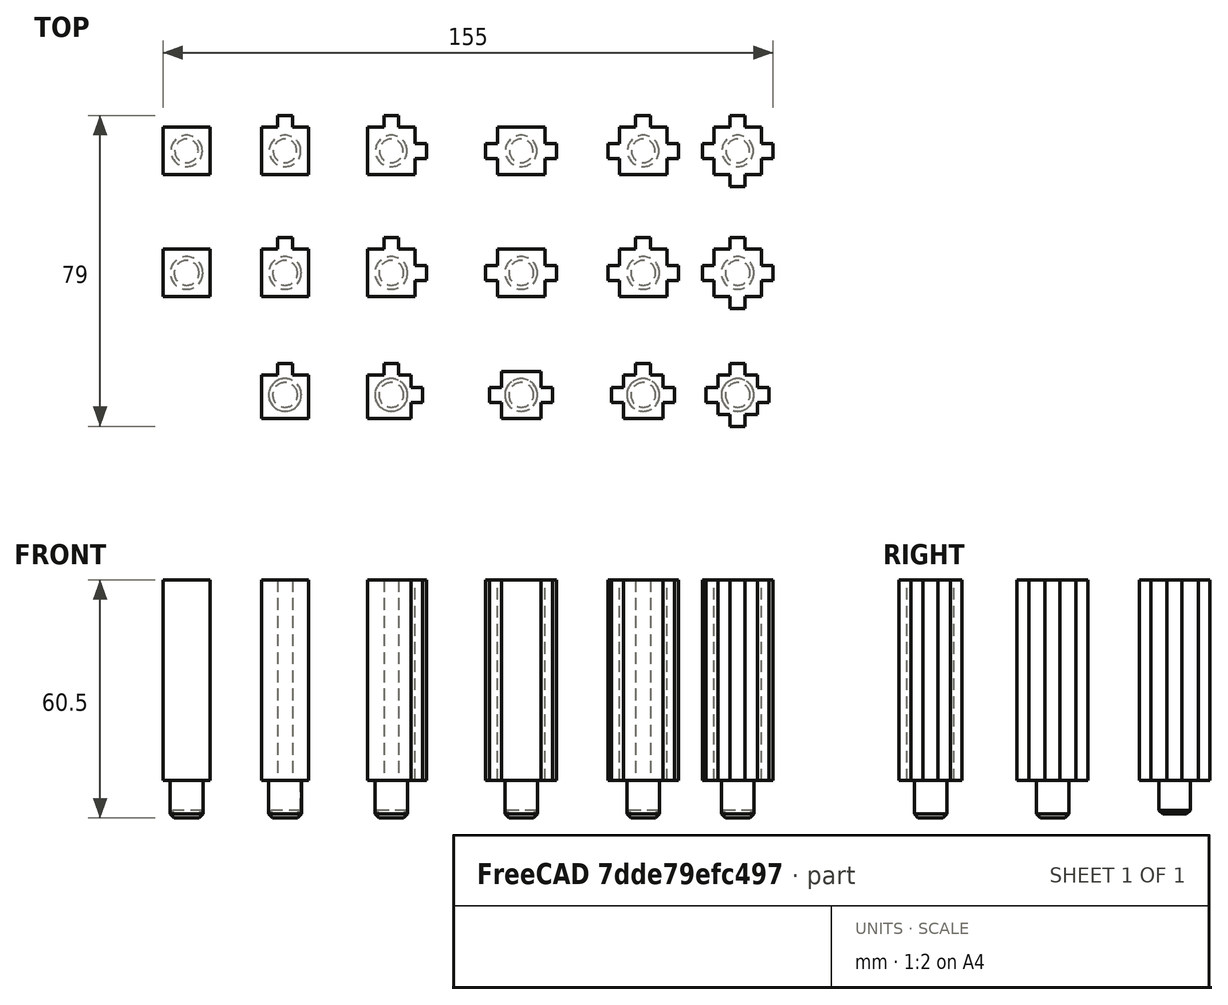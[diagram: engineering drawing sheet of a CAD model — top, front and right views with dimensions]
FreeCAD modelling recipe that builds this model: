
FCSTD DOCUMENT  (FreeCAD 0.18R16110 (Git))
Label: poste
License: All rights reserved
LicenseURL: http://en.wikipedia.org/wiki/All_rights_reserved
objects: Part::Box×53, Part::Cylinder×17, Part::Chamfer×17, Part::MultiFuse×17
note: 104 computed .brp shape members not serialized (recipe doc carries the construction recipe); baked Part::Feature solids carry a one-line shape summary decoded from their .brp

FEATURE [Part::Box] Box  label="Cubo"
  AttacherType = Attacher::AttachEngine3D
  Height = 51
  Length = 12
  Width = 12
FEATURE [Part::Box] Box002  label="Cubo002"
  AttacherType = Attacher::AttachEngine3D
  Height = 51
  Length = 3.8
  Placement = pos=(4.1,11,0) rot=(0,0,1;0rad)
  Width = 4
FEATURE [Part::Box] Box003  label="Cubo003"
  AttacherType = Attacher::AttachEngine3D
  Height = 51
  Length = 4
  Placement = pos=(-3,4.1,0) rot=(0,0,1;0rad)
  Width = 3.8
FEATURE [Part::Box] Box004  label="Cubo004"
  AttacherType = Attacher::AttachEngine3D
  Height = 51
  Length = 4
  Placement = pos=(11,4.1,0) rot=(0,0,1;0rad)
  Width = 3.8
FEATURE [Part::Cylinder] Cylinder  label="Cilindro"
  Angle = 360
  AttacherType = Attacher::AttachEngine3D
  Height = 9
  Placement = pos=(6,6,-8.5) rot=(0,0,1;0rad)
  Radius = 4
FEATURE [Part::Chamfer] Chamfer
  Base = -> Cylinder
  Edges = 1 edges r=1: [Edge3]
FEATURE [Part::MultiFuse] Fusion  label="A8_poste_3_paredes"
  Placement = pos=(27,0,0) rot=(0,0,1;0rad)
  Shapes = -> [Box,Box003,Box002,Box004,Chamfer]
FEATURE [Part::Box] Box005  label="Cubo005"
  AttacherType = Attacher::AttachEngine3D
  Height = 51
  Length = 12
  Width = 12
FEATURE [Part::Cylinder] Cylinder001  label="Cilindro001"
  Angle = 360
  AttacherType = Attacher::AttachEngine3D
  Height = 9
  Placement = pos=(6,6,-8.5) rot=(0,0,1;0rad)
  Radius = 4
FEATURE [Part::Box] Box006  label="Cubo006"
  AttacherType = Attacher::AttachEngine3D
  Height = 51
  Length = 3.8
  Placement = pos=(4.1,-3,0) rot=(0,0,1;0rad)
  Width = 4
FEATURE [Part::Box] Box007  label="Cubo007"
  AttacherType = Attacher::AttachEngine3D
  Height = 51
  Length = 4
  Placement = pos=(-3,4.1,0) rot=(0,0,1;0rad)
  Width = 3.8
FEATURE [Part::Box] Box008  label="Cubo008"
  AttacherType = Attacher::AttachEngine3D
  Height = 51
  Length = 3.8
  Placement = pos=(4.1,11,0) rot=(0,0,1;0rad)
  Width = 4
FEATURE [Part::Box] Box009  label="Cubo009"
  AttacherType = Attacher::AttachEngine3D
  Height = 51
  Length = 4
  Placement = pos=(11,4.1,0) rot=(0,0,1;0rad)
  Width = 3.8
FEATURE [Part::Chamfer] Chamfer001
  Base = -> Cylinder001
  Edges = 1 edges r=1: [Edge3]
FEATURE [Part::MultiFuse] Fusion001  label="A8_poste_4_paredes"
  Placement = pos=(51,0,0) rot=(0,0,1;0rad)
  Shapes = -> [Box005,Box006,Box007,Box008,Box009,Chamfer001]
FEATURE [Part::Box] Box010  label="Cubo010"
  AttacherType = Attacher::AttachEngine3D
  Height = 51
  Length = 12
  Width = 12
FEATURE [Part::Cylinder] Cylinder002  label="Cilindro002"
  Angle = 360
  AttacherType = Attacher::AttachEngine3D
  Height = 9
  Placement = pos=(6,6,-8.5) rot=(0,0,1;0rad)
  Radius = 4
FEATURE [Part::Box] Box012  label="Cubo012"
  AttacherType = Attacher::AttachEngine3D
  Height = 51
  Length = 3.8
  Placement = pos=(4.1,11,0) rot=(0,0,1;0rad)
  Width = 4
FEATURE [Part::Box] Box013  label="Cubo013"
  AttacherType = Attacher::AttachEngine3D
  Height = 51
  Length = 4
  Placement = pos=(11,4.1,0) rot=(0,0,1;0rad)
  Width = 3.8
FEATURE [Part::Chamfer] Chamfer002
  Base = -> Cylinder002
  Edges = 1 edges r=1: [Edge3]
FEATURE [Part::MultiFuse] Fusion002  label="A8_poste_2_paredes_esquina"
  Placement = pos=(-37,0,0) rot=(0,0,1;0rad)
  Shapes = -> [Box010,Box012,Box013,Chamfer002]
FEATURE [Part::Box] Box014  label="Cubo014"
  AttacherType = Attacher::AttachEngine3D
  Height = 51
  Length = 12
  Width = 12
FEATURE [Part::Cylinder] Cylinder003  label="Cilindro003"
  Angle = 360
  AttacherType = Attacher::AttachEngine3D
  Height = 9
  Placement = pos=(6,6,-8.5) rot=(0,0,1;0rad)
  Radius = 4
FEATURE [Part::Box] Box015  label="Cubo015"
  AttacherType = Attacher::AttachEngine3D
  Height = 51
  Length = 4
  Placement = pos=(-3,4.1,0) rot=(0,0,1;0rad)
  Width = 3.8
FEATURE [Part::Box] Box017  label="Cubo017"
  AttacherType = Attacher::AttachEngine3D
  Height = 51
  Length = 4
  Placement = pos=(11,4.1,0) rot=(0,0,1;0rad)
  Width = 3.8
FEATURE [Part::Chamfer] Chamfer003
  Base = -> Cylinder003
  Edges = 1 edges r=1: [Edge3]
FEATURE [Part::MultiFuse] Fusion003  label="A8_poste_2_paredes_linea"
  Placement = pos=(-4,0,0) rot=(0,0,1;0rad)
  Shapes = -> [Box014,Box015,Box017,Chamfer003]
FEATURE [Part::Box] Box018  label="Cubo018"
  AttacherType = Attacher::AttachEngine3D
  Height = 51
  Length = 12
  Width = 12
FEATURE [Part::Cylinder] Cylinder004  label="Cilindro004"
  Angle = 360
  AttacherType = Attacher::AttachEngine3D
  Height = 9
  Placement = pos=(6,6,-8.5) rot=(0,0,1;0rad)
  Radius = 4
FEATURE [Part::Box] Box019  label="Cubo019"
  AttacherType = Attacher::AttachEngine3D
  Height = 51
  Length = 3.8
  Placement = pos=(4.1,11,0) rot=(0,0,1;0rad)
  Width = 4
FEATURE [Part::Chamfer] Chamfer004
  Base = -> Cylinder004
  Edges = 1 edges r=1: [Edge3]
FEATURE [Part::MultiFuse] Fusion004  label="A8_poste_1_pared"
  Placement = pos=(-64,0,0) rot=(0,0,1;0rad)
  Shapes = -> [Box018,Box019,Chamfer004]
FEATURE [Part::Box] Box020  label="Cubo020"
  AttacherType = Attacher::AttachEngine3D
  Height = 51
  Length = 12
  Width = 12
FEATURE [Part::Cylinder] Cylinder005  label="Cilindro005"
  Angle = 360
  AttacherType = Attacher::AttachEngine3D
  Height = 9
  Placement = pos=(6,6,-8.5) rot=(0,0,1;0rad)
  Radius = 4
FEATURE [Part::Chamfer] Chamfer005
  Base = -> Cylinder005
  Edges = 1 edges r=1: [Edge3]
FEATURE [Part::MultiFuse] Fusion005  label="A8_poste_0_pared"
  Placement = pos=(-89,0,0) rot=(0,0,1;0rad)
  Shapes = -> [Box020,Chamfer005]
FEATURE [Part::Box] Box021  label="Cubo021"
  AttacherType = Attacher::AttachEngine3D
  Height = 51
  Length = 12
  Width = 12
FEATURE [Part::Box] Box022  label="Cubo022"
  AttacherType = Attacher::AttachEngine3D
  Height = 51
  Length = 4
  Placement = pos=(-3,4.1,0) rot=(0,0,1;0rad)
  Width = 3.8
FEATURE [Part::Box] Box023  label="Cubo023"
  AttacherType = Attacher::AttachEngine3D
  Height = 51
  Length = 3.8
  Placement = pos=(4.1,11,0) rot=(0,0,1;0rad)
  Width = 4
FEATURE [Part::Box] Box024  label="Cubo024"
  AttacherType = Attacher::AttachEngine3D
  Height = 51
  Length = 4
  Placement = pos=(11,4.1,0) rot=(0,0,1;0rad)
  Width = 3.8
FEATURE [Part::Cylinder] Cylinder006  label="Cilindro006"
  Angle = 360
  AttacherType = Attacher::AttachEngine3D
  Height = 10
  Placement = pos=(6,6,-9.5) rot=(0,0,1;0rad)
  Radius = 4.15
FEATURE [Part::Chamfer] Chamfer011
  Base = -> Cylinder006
  Edges = 1 edges r=1: [Edge3]
FEATURE [Part::MultiFuse] Fusion009  label="Prusa_poste_3_paredes"
  Placement = pos=(27,-31,0) rot=(0,0,1;0rad)
  Shapes = -> [Box021,Box022,Box023,Box024,Chamfer011]
FEATURE [Part::Box] Box025  label="Cubo025"
  AttacherType = Attacher::AttachEngine3D
  Height = 51
  Length = 12
  Width = 12
FEATURE [Part::Cylinder] Cylinder007  label="Cilindro007"
  Angle = 360
  AttacherType = Attacher::AttachEngine3D
  Height = 10
  Placement = pos=(6,6,-9.5) rot=(0,0,1;0rad)
  Radius = 4.15
FEATURE [Part::Chamfer] Chamfer006
  Base = -> Cylinder007
  Edges = 1 edges r=1: [Edge3]
FEATURE [Part::Box] Box026  label="Cubo026"
  AttacherType = Attacher::AttachEngine3D
  Height = 51
  Length = 3.8
  Placement = pos=(4.1,-3,0) rot=(0,0,1;0rad)
  Width = 4
FEATURE [Part::Box] Box027  label="Cubo027"
  AttacherType = Attacher::AttachEngine3D
  Height = 51
  Length = 4
  Placement = pos=(-3,4.1,0) rot=(0,0,1;0rad)
  Width = 3.8
FEATURE [Part::Box] Box028  label="Cubo028"
  AttacherType = Attacher::AttachEngine3D
  Height = 51
  Length = 3.8
  Placement = pos=(4.1,11,0) rot=(0,0,1;0rad)
  Width = 4
FEATURE [Part::Box] Box029  label="Cubo029"
  AttacherType = Attacher::AttachEngine3D
  Height = 51
  Length = 4
  Placement = pos=(11,4.1,0) rot=(0,0,1;0rad)
  Width = 3.8
FEATURE [Part::MultiFuse] Fusion008  label="Prusa_poste_4_paredes"
  Placement = pos=(51,-31,0) rot=(0,0,1;0rad)
  Shapes = -> [Box025,Box026,Box027,Box028,Box029,Chamfer006]
FEATURE [Part::Box] Box030  label="Cubo030"
  AttacherType = Attacher::AttachEngine3D
  Height = 51
  Length = 12
  Width = 12
FEATURE [Part::Cylinder] Cylinder008  label="Cilindro008"
  Angle = 360
  AttacherType = Attacher::AttachEngine3D
  Height = 10
  Placement = pos=(6,6,-9.5) rot=(0,0,1;0rad)
  Radius = 4.15
FEATURE [Part::Chamfer] Chamfer010
  Base = -> Cylinder008
  Edges = 1 edges r=1: [Edge3]
FEATURE [Part::Box] Box031  label="Cubo031"
  AttacherType = Attacher::AttachEngine3D
  Height = 51
  Length = 3.8
  Placement = pos=(4.1,11,0) rot=(0,0,1;0rad)
  Width = 4
FEATURE [Part::Box] Box032  label="Cubo032"
  AttacherType = Attacher::AttachEngine3D
  Height = 51
  Length = 4
  Placement = pos=(11,4.1,0) rot=(0,0,1;0rad)
  Width = 3.8
FEATURE [Part::MultiFuse] Fusion006  label="Prusa_poste_2_paredes_esquina"
  Placement = pos=(-37,-31,0) rot=(0,0,1;0rad)
  Shapes = -> [Box030,Box031,Box032,Chamfer010]
FEATURE [Part::Box] Box033  label="Cubo033"
  AttacherType = Attacher::AttachEngine3D
  Height = 51
  Length = 12
  Width = 12
FEATURE [Part::Cylinder] Cylinder009  label="Cilindro009"
  Angle = 360
  AttacherType = Attacher::AttachEngine3D
  Height = 10
  Placement = pos=(6,6,-9.5) rot=(0,0,1;0rad)
  Radius = 4.15
FEATURE [Part::Chamfer] Chamfer009
  Base = -> Cylinder009
  Edges = 1 edges r=1: [Edge3]
FEATURE [Part::Box] Box034  label="Cubo034"
  AttacherType = Attacher::AttachEngine3D
  Height = 51
  Length = 4
  Placement = pos=(-3,4.1,0) rot=(0,0,1;0rad)
  Width = 3.8
FEATURE [Part::Box] Box035  label="Cubo035"
  AttacherType = Attacher::AttachEngine3D
  Height = 51
  Length = 4
  Placement = pos=(11,4.1,0) rot=(0,0,1;0rad)
  Width = 3.8
FEATURE [Part::MultiFuse] Fusion007  label="Prusa_poste_2_paredes_linea"
  Placement = pos=(-4,-31,0) rot=(0,0,1;0rad)
  Shapes = -> [Box033,Box034,Box035,Chamfer009]
FEATURE [Part::Box] Box036  label="Cubo036"
  AttacherType = Attacher::AttachEngine3D
  Height = 51
  Length = 12
  Width = 12
FEATURE [Part::Cylinder] Cylinder010  label="Cilindro010"
  Angle = 360
  AttacherType = Attacher::AttachEngine3D
  Height = 10
  Placement = pos=(6,6,-9.5) rot=(0,0,1;0rad)
  Radius = 4.15
FEATURE [Part::Chamfer] Chamfer008
  Base = -> Cylinder010
  Edges = 1 edges r=1: [Edge3]
FEATURE [Part::Box] Box037  label="Cubo037"
  AttacherType = Attacher::AttachEngine3D
  Height = 51
  Length = 3.8
  Placement = pos=(4.1,11,0) rot=(0,0,1;0rad)
  Width = 4
FEATURE [Part::MultiFuse] Fusion011  label="Prusa_poste_1_pared"
  Placement = pos=(-64,-31,0) rot=(0,0,1;0rad)
  Shapes = -> [Box036,Box037,Chamfer008]
FEATURE [Part::Box] Box038  label="Cubo038"
  AttacherType = Attacher::AttachEngine3D
  Height = 51
  Length = 12
  Width = 12
FEATURE [Part::Cylinder] Cylinder011  label="Cilindro011"
  Angle = 360
  AttacherType = Attacher::AttachEngine3D
  Height = 10
  Placement = pos=(6,6,-9.5) rot=(0,0,1;0rad)
  Radius = 4.15
FEATURE [Part::Chamfer] Chamfer007
  Base = -> Cylinder011
  Edges = 1 edges r=1: [Edge3]
FEATURE [Part::MultiFuse] Fusion010  label="Prusa_poste_0_pared"
  Placement = pos=(-89,-31,0) rot=(0,0,1;0rad)
  Shapes = -> [Box038,Chamfer007]
FEATURE [Part::Box] Box039  label="Cubo039"
  AttacherType = Attacher::AttachEngine3D
  Height = 51
  Length = 10
  Placement = pos=(1,0,0) rot=(0,0,1;0rad)
  Width = 11
FEATURE [Part::Box] Box040  label="Cubo040"
  AttacherType = Attacher::AttachEngine3D
  Height = 51
  Length = 4
  Placement = pos=(-2,4.1,0) rot=(0,0,1;0rad)
  Width = 3.8
FEATURE [Part::Box] Box041  label="Cubo041"
  AttacherType = Attacher::AttachEngine3D
  Height = 51
  Length = 3.8
  Placement = pos=(4.1,10,0) rot=(0,0,1;0rad)
  Width = 4
FEATURE [Part::Box] Box042  label="Cubo042"
  AttacherType = Attacher::AttachEngine3D
  Height = 51
  Length = 4
  Placement = pos=(10,4.1,0) rot=(0,0,1;0rad)
  Width = 3.8
FEATURE [Part::Cylinder] Cylinder012  label="Cilindro012"
  Angle = 360
  AttacherType = Attacher::AttachEngine3D
  Height = 10
  Placement = pos=(6,6,-9.5) rot=(0,0,1;0rad)
  Radius = 4.15
FEATURE [Part::Chamfer] Chamfer016
  Base = -> Cylinder012
  Edges = 1 edges r=1: [Edge3]
FEATURE [Part::MultiFuse] Fusion015  label="Prusa_poste_recortado_3_paredes"
  Placement = pos=(27,-62,0) rot=(0,0,1;0rad)
  Shapes = -> [Box039,Box040,Box041,Box042,Chamfer016]
FEATURE [Part::Box] Box043  label="Cubo043"
  AttacherType = Attacher::AttachEngine3D
  Height = 51
  Length = 10
  Placement = pos=(1,1,0) rot=(0,0,1;0rad)
  Width = 10
FEATURE [Part::Cylinder] Cylinder013  label="Cilindro013"
  Angle = 360
  AttacherType = Attacher::AttachEngine3D
  Height = 10
  Placement = pos=(6,6,-9.5) rot=(0,0,1;0rad)
  Radius = 4.15
FEATURE [Part::Chamfer] Chamfer012
  Base = -> Cylinder013
  Edges = 1 edges r=1: [Edge3]
FEATURE [Part::Box] Box044  label="Cubo044"
  AttacherType = Attacher::AttachEngine3D
  Height = 51
  Length = 3.8
  Placement = pos=(4.1,-2,0) rot=(0,0,1;0rad)
  Width = 4
FEATURE [Part::Box] Box045  label="Cubo045"
  AttacherType = Attacher::AttachEngine3D
  Height = 51
  Length = 4
  Placement = pos=(-2,4.1,0) rot=(0,0,1;0rad)
  Width = 3.8
FEATURE [Part::Box] Box046  label="Cubo046"
  AttacherType = Attacher::AttachEngine3D
  Height = 51
  Length = 3.8
  Placement = pos=(4.1,10,0) rot=(0,0,1;0rad)
  Width = 4
FEATURE [Part::Box] Box047  label="Cubo047"
  AttacherType = Attacher::AttachEngine3D
  Height = 51
  Length = 4
  Placement = pos=(10,4.1,0) rot=(0,0,1;0rad)
  Width = 3.8
FEATURE [Part::MultiFuse] Fusion014  label="Prusa_poste_recortado_4_paredes"
  Placement = pos=(51,-62,0) rot=(0,0,1;0rad)
  Shapes = -> [Box043,Box044,Box045,Box046,Box047,Chamfer012]
FEATURE [Part::Box] Box048  label="Cubo048"
  AttacherType = Attacher::AttachEngine3D
  Height = 51
  Length = 11
  Width = 11
FEATURE [Part::Cylinder] Cylinder014  label="Cilindro014"
  Angle = 360
  AttacherType = Attacher::AttachEngine3D
  Height = 10
  Placement = pos=(6,6,-9.5) rot=(0,0,1;0rad)
  Radius = 4.15
FEATURE [Part::Chamfer] Chamfer015
  Base = -> Cylinder014
  Edges = 1 edges r=1: [Edge3]
FEATURE [Part::Box] Box049  label="Cubo049"
  AttacherType = Attacher::AttachEngine3D
  Height = 51
  Length = 3.8
  Placement = pos=(4.1,10,0) rot=(0,0,1;0rad)
  Width = 4
FEATURE [Part::Box] Box050  label="Cubo050"
  AttacherType = Attacher::AttachEngine3D
  Height = 51
  Length = 4
  Placement = pos=(10,4.1,0) rot=(0,0,1;0rad)
  Width = 3.8
FEATURE [Part::MultiFuse] Fusion012  label="Prusa_poste_recortado_2_paredes_esquina"
  Placement = pos=(-37,-62,0) rot=(0,0,1;0rad)
  Shapes = -> [Box048,Box049,Box050,Chamfer015]
FEATURE [Part::Box] Box051  label="Cubo051"
  AttacherType = Attacher::AttachEngine3D
  Height = 51
  Length = 10
  Placement = pos=(1,0,0) rot=(0,0,1;0rad)
  Width = 12
FEATURE [Part::Cylinder] Cylinder015  label="Cilindro015"
  Angle = 360
  AttacherType = Attacher::AttachEngine3D
  Height = 10
  Placement = pos=(6,6,-9.5) rot=(0,0,1;0rad)
  Radius = 4.15
FEATURE [Part::Chamfer] Chamfer014
  Base = -> Cylinder015
  Edges = 1 edges r=1: [Edge3]
FEATURE [Part::Box] Box052  label="Cubo052"
  AttacherType = Attacher::AttachEngine3D
  Height = 51
  Length = 4
  Placement = pos=(-2,4.1,0) rot=(0,0,1;0rad)
  Width = 3.8
FEATURE [Part::Box] Box053  label="Cubo053"
  AttacherType = Attacher::AttachEngine3D
  Height = 51
  Length = 4
  Placement = pos=(10,4.1,0) rot=(0,0,1;0rad)
  Width = 3.8
FEATURE [Part::MultiFuse] Fusion013  label="Prusa_poste_recortado_2_paredes_linea"
  Placement = pos=(-4,-62,0) rot=(0,0,1;0rad)
  Shapes = -> [Box051,Box052,Box053,Chamfer014]
FEATURE [Part::Box] Box054  label="Cubo054"
  AttacherType = Attacher::AttachEngine3D
  Height = 51
  Length = 12
  Width = 11
FEATURE [Part::Cylinder] Cylinder016  label="Cilindro016"
  Angle = 360
  AttacherType = Attacher::AttachEngine3D
  Height = 10
  Placement = pos=(6,6,-9.5) rot=(0,0,1;0rad)
  Radius = 4.15
FEATURE [Part::Chamfer] Chamfer013
  Base = -> Cylinder016
  Edges = 1 edges r=1: [Edge3]
FEATURE [Part::Box] Box055  label="Cubo055"
  AttacherType = Attacher::AttachEngine3D
  Height = 51
  Length = 3.8
  Placement = pos=(4.1,10,0) rot=(0,0,1;0rad)
  Width = 4
FEATURE [Part::MultiFuse] Fusion016  label="Prusa_poste_recortado_1_pared"
  Placement = pos=(-64,-62,0) rot=(0,0,1;0rad)
  Shapes = -> [Box054,Box055,Chamfer013]
